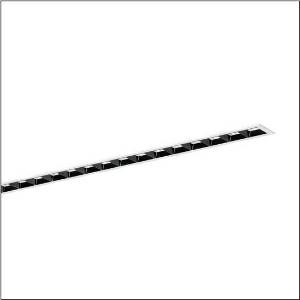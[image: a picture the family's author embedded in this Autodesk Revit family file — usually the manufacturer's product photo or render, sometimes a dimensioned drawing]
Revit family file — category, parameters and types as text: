
# Revit family: silica_r__21_51mx12tbt5w_1d14
name_source: partatom
category: Lighting Fixtures
units: mm (PartAtom-declared; Revit-internal decimal feet)

## family parameters
Cut with Voids When Loaded = No
Host = Face
Light Source = No
Part Type = Normal
Room Calculation Point = No
Round Connector Dimension = Use Diameter
Shared = No

## types (1)
- --- (1 x LED, 4650 lm, 40.2 W, 6500K)
    Apparent Load = 40 VA
    CIE Flux Codes = 84 100 100 100 100
    Color Rendering = 80
    Color Temperature = 6500K
    Default Elevation = 1800 mm
    Description = Silica® 21, office luminaire, primary light control with darklight reflector, of PMMA, black, CAT 2 (L<= 3000cd/m²), light emission: direct distribution, primary light characteristic: symmetric, installation type: recessed, LED, rated luminous flux: 4.650lm, luminous efficacy: 110lm/W, light colour: 8tw, colour temperature: 2700..6500K, control gear: DALI DT8, with terminal, 3+2-pole, max. 2.5mm², mains connection: 220..240V, AC, 50/60Hz, rated input power: 42.2W, luminaire housing, of aluminium, traffic white (RAL 9016), length: 1.528mm, width: 79mm, height: 53mm, protection rating (complete): IP20, insulation class (complete): insulation class I (protective earthing), certification: CE, ENEC, VDE, permissible operating ambient temperature: 0..+35°C, standard: EN 50419, packaging unit: 1 piece
    Height = 0 mm  [stored 0 ft]
    Lamp = 1 x LED
    Lamp Light Flux = 4650 lm
    Lamp Power = 40.2 W
    Lamp count = 1
    Length = 1527 mm
    Luminous efficacy = 116 lm/W
    Manufacturer = Siteco
    ModVariant = No
    Model = 51MX12TBT5W
    Mounting Place = Ceiling
    Mounting Type = Recessed
    Number of Poles = 1
    OnlyDefault = Yes
    Power Factor = 1
    Product Name = Silica® 21
    Product group = office luminaire | ceiling recessed
    ProductGroupID = 401
    Protection Class = Protection class I
    Protection Degree = IP 20
    RLX_Detail_Level = 1
    RLX_Emergency_Light_Flux = 0 lm
    RLX_Emergency_Type = 0
    RLX_Emergency_Type_DB = No
    RlxData = <blob elided: 39365 chars, md5=f244f065>
    Socket = socket
    Standby Power = 0 W
    System Light Flux = 4650 lm
    System Power = 40 W
    Type Comments = individual setting
    Type Image = l_1335880.jpg
    URL = http://relux.com
    VarID = @adj_140172
    Voltage = 0 V
    Weight = 0.00 kg
    Width = 79 mm

note: [stored X ft] marks values corroborated as IEEE doubles in the binary element streams (Revit-internal decimal feet)

## geometry (parser evidence)
native form markers: Blend x4, Sweep x10
no freeform markers — native parametric forms only
